# Revit family: IS_Connect_E5675_BIM_DE
name_source: partatom
category: Plumbing Fixtures
revit_build: Autodesk Revit MEP 2016 (Build: 20161004_0715(x64)
units: mm (PartAtom-declared; Revit-internal decimal feet)

## family parameters
Always vertical = No
Cut with Voids When Loaded = No
OmniClass Number = 23.45.05.21.11.21
OmniClass Title = Urinals
Part Type = Normal
Room Calculation Point = No
Round Connector Dimension = Use Diameter
Shared = No
Work Plane-Based = No

## types (2) — shared parameters
Accessories = www.idealstandard.de\ersatzteile
AreaUnits = millimeters
AssetType = Fixed
BIMobject category = Urinals
BOSUseNativeGeometries = 1
Brand = Ideal Standard
Brand url = http://www.idealstandard.co.uk
CodePerformance = 0
ConnectionType = Plumbing
CurrencyUnit = €
CurrentRevision = 1
Date of publishing = 2017_11_20
DurationUnit = year
Edition number = 1
ExpectedLife = 25
Features = CONNECT urinal 325x315mm
IFC Classification = Sanitary Terminal
IfcExportAs = IfcSanitaryTerminalType
IfcExportType = URINALS
Installation instructions = http://www.idealstandard.de
InstallationInstructions = www.idealstandard.de\produkte
LinearUnits = millimeters
Manufacturer name = Ideal Standard
ManufacturerURL = www.idealstandard.com
Material = Vitreous china
Material main = Ceramics
NBS Reference Code = 35-93-82
NBS Reference Description = Wall-Hung Urinals
NettWeight = 16,7 kg
Nominal height = 650
Nominal width = 325
NominalDepth = 311 mm  [stored 1.02034 ft]
NominalHeight = 646 mm
NominalLength = 311 mm  [stored 1.02034 ft]
NominalWidth = 325 mm  [stored 1.06627 ft]
OmniClass Code = 23-31 21 00
OmniClass Description = Urinals
Product Guid = f12050ec-0a7c-4ae5-a88c-cb50ebfe3456
Product SKU = E5675
Product data url = https://bimobject.com
Product family = CONNECT
Product group = Urinal
Product name = CONNECT urinal 325x315mm
Product url = http://www.idealstandard.de
ProductInformation = www.idealstandard.de/produkte
QR code = http://bimobject.com
Shape = Sculptured
Size = 325x311x646 mm
Space = Internal
SpareParts = www.idealstandard.de/ersatzteile
Technical description = http://www.idealstandard.de
URL = http://www.idealstandard.de
Uniclass 2.0 Code = PR-35-93-82
Uniclass 2.0 Description = Wall-Hung Urinals
Uniclass 2015 Code = Pr_40_20_93_82
Uniclass 2015 Name = Wall-hung urinals
Uniclass2015Code = Pr_40_20_93_82
Uniclass2015Title = Wall-hung urinals
Uniclass2015Version = Products v1.1
UrinalMaterial = Vitreous china
Version = 1
VolumeUnits = Litres
Weight Net (Kg) = 16.7
zero-valued in all types: Cost, SpilloverLevel

## per-type parameters (varying)
| type | BIMObjectName | BarCode | Color | EAN code | Finish | MainColor | Model | ModelNumber | Name | UrinalColor |
| E567501 CONNECT urinal 325x315mm | ISI_IdealStandard_WallHungUrinals_Connect_E567501 | 5017830480532 | White | 5017830480532 | White | White | E567501 | E567501 | WallHungUrinals_Connect_E567501_IdealStandard | White |
| E5675MA CONNECT urinal 325x315mm | ISI_IdealStandard_WallHungUrinals_Connect_E5675MA | 5017830480549 | WHITE IP | 5017830480549 | WHITE IP | WHITE IP | E5675MA | E5675MA | WallHungUrinals_Connect_E5675MA_IdealStandard | WHITE IP |

note: column(s) folded — value = type name in every type: Description, ModelReference

note: [stored X ft] marks values corroborated as IEEE doubles in the binary element streams (Revit-internal decimal feet)

## geometry (parser evidence)
native form markers: Blend x4, Sweep x1
no freeform markers — native parametric forms only
